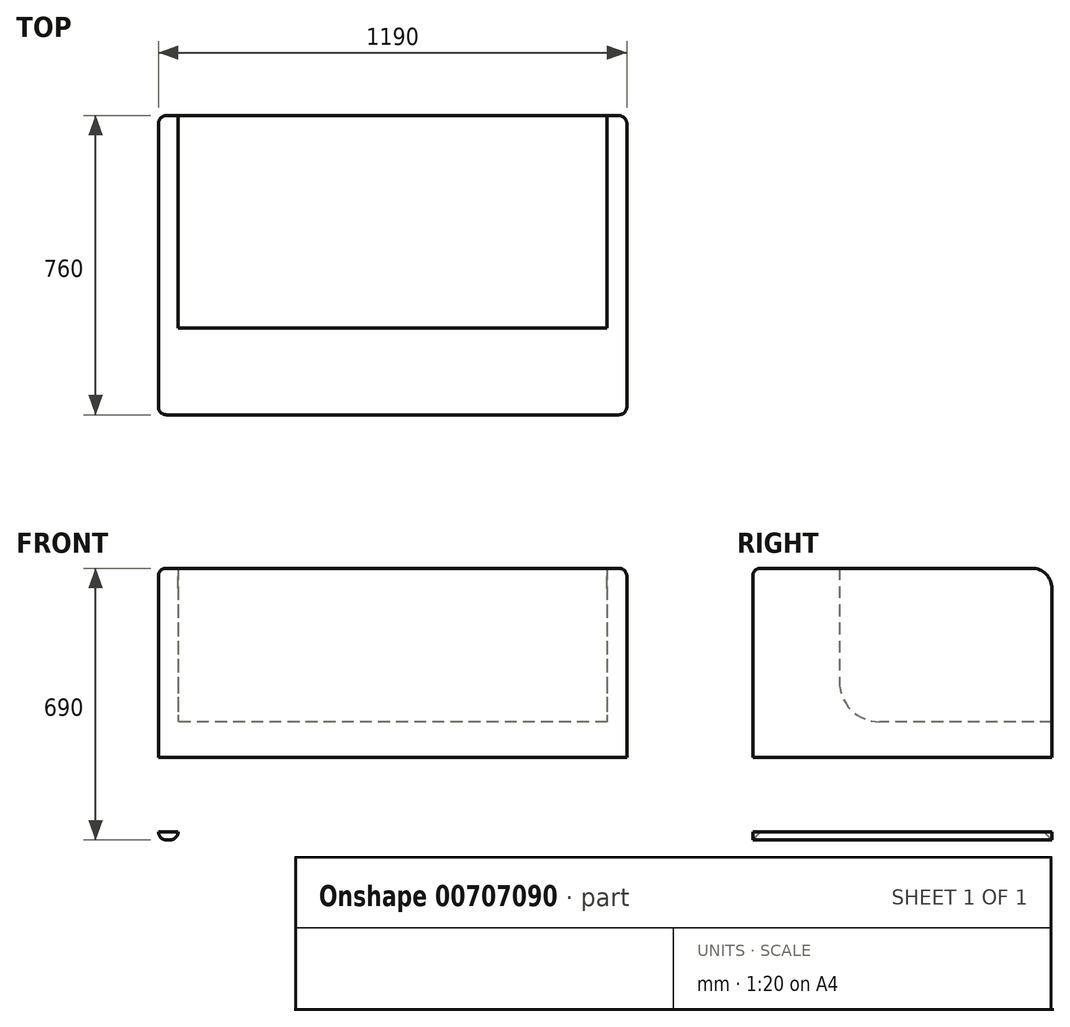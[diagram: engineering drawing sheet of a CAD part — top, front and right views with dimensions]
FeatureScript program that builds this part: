
annotation { "Feature Type Name" : "Feature", "Feature Type Description" : "" }
export const myFeature = defineFeature(function(context is Context, id is Id, definition is map)
    precondition{}
    {
        {
            var Q0;
            Q0=qCreatedBy(makeId("Right.planeOp"),FACE);
            var sketch = newSketch(context, id + "F0", { "sketchPlane" : qUnion([Q0])});
            skLineSegment(sketch, "E0", {"start": v(0, 0) * mm, "end": v(760, 0) * mm});
            skLineSegment(sketch, "E1", {"start": v(760, 0) * mm, "end": v(760, 690) * mm});
            skLineSegment(sketch, "E2", {"start": v(760, 690) * mm, "end": v(0, 690) * mm});
            skLineSegment(sketch, "E3", {"start": v(0, 690) * mm, "end": v(0, 0) * mm});
            skSolve(sketch);
        }
        {
            var Q0;
            Q0=makeQuery(id+"F0.imprint","IMPRINT",FACE,{"disambiguationData":[TD([[makeQuery(id+"F0.imprint","IMPRINT",EDGE,{"derivedFrom":sQuery(id+"F0.wireOp",EDGE,"E0")}),1.0]])]});
            extrude(context, id + "F1", {"entities" : qUnion([Q0]), "depth" : 1190 * mm});
        }
        {
            var Q0;
            Q0=makeQuery(id+"F1.opExtrude","SWEPT_FACE",FACE,{"disambiguationData":[OSD([sQuery(id+"F0.wireOp",EDGE,"E1")])]});
            var sketch = newSketch(context, id + "F2", { "sketchPlane" : qUnion([Q0])});
            skLineSegment(sketch, "E4.bottom", {"start": v(-1140, 0) * mm, "end": v(-50, 0) * mm});
            skLineSegment(sketch, "E4.top", {"start": v(-1140, 210) * mm, "end": v(-50, 210) * mm});
            skLineSegment(sketch, "E4.left", {"start": v(-1140, 0) * mm, "end": v(-1140, 210) * mm});
            skLineSegment(sketch, "E4.right", {"start": v(-50, 0) * mm, "end": v(-50, 210) * mm});
            skSolve(sketch);
        }
        {
            var Q0;
            Q0=makeQuery(id+"F2.imprint","IMPRINT",FACE,{"disambiguationData":[TD([[makeQuery(id+"F2.imprint","IMPRINT",EDGE,{"derivedFrom":sQuery(id+"F2.wireOp",EDGE,"E4.bottom")}),1.0]])]});
            var Q1;
            Q1=makeQuery(id+"F1.opExtrude","SWEPT_FACE",FACE,{"disambiguationData":[OSD([sQuery(id+"F0.wireOp",EDGE,"E3")])]});
            extrude(context, id + "F3", {"entities" : qUnion([Q0]), "operationType" : NewBodyOperationType.REMOVE, "endBound" : BoundingType.UP_TO_SURFACE, "oppositeDirection" : true, "endBoundEntityFace" : qUnion([Q1]), "depth" : 25.4 * mm});
        }
        {
            var Q0;
            Q0=qCreatedBy(makeId("Right.planeOp"),FACE);
            var sketch = newSketch(context, id + "F4", { "sketchPlane" : qUnion([Q0])});
            skPoint(sketch, "E5.0", {"position": v(760, 690) * mm});
            skLineSegment(sketch, "E6.bottom", {"start": v(760, 690) * mm, "end": v(220, 690) * mm});
            skLineSegment(sketch, "E6.top", {"start": v(760, 300) * mm, "end": v(220, 300) * mm});
            skLineSegment(sketch, "E6.left", {"start": v(760, 690) * mm, "end": v(760, 300) * mm});
            skLineSegment(sketch, "E6.right", {"start": v(220, 690) * mm, "end": v(220, 300) * mm});
            skSolve(sketch);
        }
        {
            var Q0;
            Q0=makeQuery(id+"F4.imprint","IMPRINT",FACE,{"disambiguationData":[TD([[makeQuery(id+"F4.imprint","IMPRINT",EDGE,{"derivedFrom":sQuery(id+"F4.wireOp",EDGE,"E6.bottom")}),1.0]])]});
            extrude(context, id + "F5", {"entities" : qUnion([Q0]), "operationType" : NewBodyOperationType.REMOVE, "depth" : 1140 * mm, "hasSecondDirection" : true, "secondDirectionOppositeDirection" : false, "secondDirectionDepth" : 50 * mm});
        }
        {
            var Q0;
            Q0=makeQuery(id+"F1.opExtrude","CAP_FACE",FACE,{"disambiguationData":[OSD([sQuery(id+"F0.wireOp",EDGE,"E0"),sQuery(id+"F0.wireOp",EDGE,"E1"),sQuery(id+"F0.wireOp",EDGE,"E2"),sQuery(id+"F0.wireOp",EDGE,"E3")])],"isStart":true});
            var Q1;
            Q1=makeQuery(id+"F1.opExtrude","CAP_FACE",FACE,{"disambiguationData":[OSD([sQuery(id+"F0.wireOp",EDGE,"E0"),sQuery(id+"F0.wireOp",EDGE,"E1"),sQuery(id+"F0.wireOp",EDGE,"E2"),sQuery(id+"F0.wireOp",EDGE,"E3")])],"isStart":false});
            var Q2;
            Q2=makeQuery(id+"F3.boolean.opBoolean","COPY",EDGE,{"derivedFrom":makeQuery(id+"F3.opExtrude","CAP_EDGE",EDGE,{"disambiguationData":[OSD([sQuery(id+"F2.wireOp",EDGE,"E4.left")])],"isStart":true})});
            var Q3;
            Q3=makeQuery(id+"F3.boolean.opBoolean","COPY",EDGE,{"derivedFrom":makeQuery(id+"F3.opExtrude","CAP_EDGE",EDGE,{"disambiguationData":[OSD([sQuery(id+"F2.wireOp",EDGE,"E4.right")])],"isStart":true})});
            var Q4;
            Q4=makeQuery(id+"F3.boolean.opBoolean","COPY",EDGE,{"derivedFrom":makeQuery(id+"F3.opExtrude","CAP_EDGE",EDGE,{"disambiguationData":[OSD([sQuery(id+"F2.wireOp",EDGE,"E4.right")])],"isStart":false})});
            var Q5;
            Q5=makeQuery(id+"F3.boolean.opBoolean","COPY",EDGE,{"derivedFrom":makeQuery(id+"F3.opExtrude","SWEPT_EDGE",EDGE,{"disambiguationData":[OSD([sQuery(id+"F0.wireOp",EDGE,"E0"),sQuery(id+"F0.wireOp",EDGE,"E1"),sQuery(id+"F2.wireOp",EDGE,"E4.bottom"),sQuery(id+"F2.wireOp",EDGE,"E4.right")])]})});
            var Q6;
            Q6=makeQuery(id+"F3.boolean.opBoolean","COPY",EDGE,{"derivedFrom":makeQuery(id+"F3.opExtrude","SWEPT_EDGE",EDGE,{"disambiguationData":[OSD([sQuery(id+"F0.wireOp",EDGE,"E0"),sQuery(id+"F0.wireOp",EDGE,"E1"),sQuery(id+"F2.wireOp",EDGE,"E4.bottom"),sQuery(id+"F2.wireOp",EDGE,"E4.left")])]})});
            var Q7;
            Q7=makeQuery(id+"F3.boolean.opBoolean","COPY",EDGE,{"derivedFrom":makeQuery(id+"F3.opExtrude","CAP_EDGE",EDGE,{"disambiguationData":[OSD([sQuery(id+"F2.wireOp",EDGE,"E4.top")])],"isStart":true})});
            var Q8;
            Q8=makeQuery(id+"F3.boolean.opBoolean","COPY",EDGE,{"derivedFrom":makeQuery(id+"F3.opExtrude","CAP_EDGE",EDGE,{"disambiguationData":[OSD([sQuery(id+"F2.wireOp",EDGE,"E4.top")])],"isStart":false})});
            var Q9;
            Q9=makeQuery(id+"F5.boolean.opBoolean","COPY",EDGE,{"derivedFrom":makeQuery(id+"F5.opExtrude","SWEPT_EDGE",EDGE,{"disambiguationData":[OSD([sQuery(id+"F4.wireOp",EDGE,"E6.top"),sQuery(id+"F4.wireOp",EDGE,"E6.left")])]})});
            var Q10;
            Q10=makeQuery(id+"F5.boolean.opBoolean","COPY",EDGE,{"derivedFrom":makeQuery(id+"F5.opExtrude","CAP_EDGE",EDGE,{"disambiguationData":[OSD([sQuery(id+"F4.wireOp",EDGE,"E6.left")])],"isStart":false})});
            var Q11;
            Q11=makeQuery(id+"F5.boolean.opBoolean","COPY",EDGE,{"derivedFrom":makeQuery(id+"F5.opExtrude","CAP_EDGE",EDGE,{"disambiguationData":[OSD([sQuery(id+"F4.wireOp",EDGE,"E6.bottom")])],"isStart":false})});
            var Q12;
            Q12=makeQuery(id+"F5.boolean.opBoolean","COPY",EDGE,{"derivedFrom":makeQuery(id+"F5.opExtrude","CAP_EDGE",EDGE,{"disambiguationData":[OSD([sQuery(id+"F4.wireOp",EDGE,"E6.bottom")])],"isStart":true})});
            var Q13;
            Q13=makeQuery(id+"F5.boolean.opBoolean","COPY",EDGE,{"derivedFrom":makeQuery(id+"F5.opExtrude","CAP_EDGE",EDGE,{"disambiguationData":[OSD([sQuery(id+"F4.wireOp",EDGE,"E6.left")])],"isStart":true})});
            var Q14;
            Q14=makeQuery(id+"F1.opExtrude","SWEPT_EDGE",EDGE,{"disambiguationData":[OSD([sQuery(id+"F0.wireOp",EDGE,"E2"),sQuery(id+"F0.wireOp",EDGE,"E3")])]});
            var Q15;
            Q15=makeQuery(id+"F3.boolean.opBoolean","COPY",EDGE,{"derivedFrom":makeQuery(id+"F3.opExtrude","CAP_EDGE",EDGE,{"disambiguationData":[OSD([sQuery(id+"F2.wireOp",EDGE,"E4.left")])],"isStart":false})});
            fillet(context, id + "F6", {"entities" : qUnion([Q0, Q1, Q2, Q3, Q4, Q5, Q6, Q7, Q8, Q9, Q10, Q11, Q12, Q13, Q14, Q15]), "radius" : 20.32 * mm, "tangentPropagation" : true, "allowEdgeOverflow" : false});
        }
        {
            var Q0;
            Q0=makeQuery(id+"F5.boolean.opBoolean","COPY",EDGE,{"derivedFrom":makeQuery(id+"F5.opExtrude","SWEPT_EDGE",EDGE,{"disambiguationData":[OSD([sQuery(id+"F4.wireOp",EDGE,"E6.bottom"),sQuery(id+"F4.wireOp",EDGE,"E6.right")])]})});
            var Q1;
            Q1=makeQuery(id+"F5.boolean.opBoolean","COPY",EDGE,{"derivedFrom":makeQuery(id+"F5.opExtrude","SWEPT_EDGE",EDGE,{"disambiguationData":[OSD([sQuery(id+"F4.wireOp",EDGE,"E6.top"),sQuery(id+"F4.wireOp",EDGE,"E6.right")])]})});
            fillet(context, id + "F7", {"entities" : qUnion([Q0, Q1]), "radius" : 101.6 * mm, "tangentPropagation" : true, "allowEdgeOverflow" : false});
        }
        {
            var Q0;
            Q0=makeQuery(id+"F3.boolean.opBoolean","COPY",FACE,{"derivedFrom":makeQuery(id+"F3.opExtrude","SWEPT_FACE",FACE,{"disambiguationData":[OSD([sQuery(id+"F2.wireOp",EDGE,"E4.left")])]})});
            var Q1;
            Q1=makeQuery(id+"F1.opExtrude","CAP_FACE",FACE,{"disambiguationData":[OSD([sQuery(id+"F0.wireOp",EDGE,"E0"),sQuery(id+"F0.wireOp",EDGE,"E1"),sQuery(id+"F0.wireOp",EDGE,"E2"),sQuery(id+"F0.wireOp",EDGE,"E3")])],"isStart":false});
            extrude(context, id + "F8", {"entities" : qUnion([Q0]), "operationType" : NewBodyOperationType.REMOVE, "endBound" : BoundingType.UP_TO_SURFACE, "oppositeDirection" : true, "endBoundEntityFace" : qUnion([Q1]), "depth" : 25.4 * mm});
        }
        {
            var Q0;
            Q0=makeQuery(id+"F3.boolean.opBoolean","COPY",FACE,{"derivedFrom":makeQuery(id+"F3.opExtrude","SWEPT_FACE",FACE,{"disambiguationData":[OSD([sQuery(id+"F2.wireOp",EDGE,"E4.right")])]})});
            var Q1;
            Q1=makeQuery(id+"F1.opExtrude","CAP_FACE",FACE,{"disambiguationData":[OSD([sQuery(id+"F0.wireOp",EDGE,"E0"),sQuery(id+"F0.wireOp",EDGE,"E1"),sQuery(id+"F0.wireOp",EDGE,"E2"),sQuery(id+"F0.wireOp",EDGE,"E3")])],"isStart":true});
            extrude(context, id + "F9", {"entities" : qUnion([Q0]), "operationType" : NewBodyOperationType.REMOVE, "endBound" : BoundingType.UP_TO_SURFACE, "oppositeDirection" : true, "endBoundEntityFace" : qUnion([Q1]), "depth" : 25.4 * mm});
        }
        {
            var Q0;
            {var subQ0=sQuery(id+"F0.wireOp",EDGE,"E2");var subQ1=sQuery(id+"F0.wireOp",EDGE,"E1");Q0=makeQuery(id+"F5.boolean.opBoolean","SPLIT",EDGE,{"disambiguationData":[TD([makeQuery(id+"F1.opExtrude","CAP_FACE",FACE,{"disambiguationData":[OSD([sQuery(id+"F0.wireOp",EDGE,"E0"),subQ1,subQ0,sQuery(id+"F0.wireOp",EDGE,"E3")])],"isStart":false})])],"derivedFrom":makeQuery(id+"F1.opExtrude","SWEPT_EDGE",EDGE,{"disambiguationData":[OSD([subQ1,subQ0])]})});}
            var Q1;
            {var subQ0=sQuery(id+"F0.wireOp",EDGE,"E2");var subQ1=sQuery(id+"F0.wireOp",EDGE,"E1");Q1=makeQuery(id+"F5.boolean.opBoolean","SPLIT",EDGE,{"disambiguationData":[TD([makeQuery(id+"F1.opExtrude","CAP_FACE",FACE,{"disambiguationData":[OSD([sQuery(id+"F0.wireOp",EDGE,"E0"),subQ1,subQ0,sQuery(id+"F0.wireOp",EDGE,"E3")])],"isStart":true})])],"derivedFrom":makeQuery(id+"F1.opExtrude","SWEPT_EDGE",EDGE,{"disambiguationData":[OSD([subQ1,subQ0])]})});}
            var Q2;
            {var subQ0=sQuery(id+"F2.wireOp",EDGE,"E4.right");var subQ1=sQuery(id+"F2.wireOp",EDGE,"E4.bottom");var subQ2=sQuery(id+"F0.wireOp",EDGE,"E1");var subQ3=sQuery(id+"F0.wireOp",EDGE,"E0");Q2=makeQuery(id+"F9.boolean.opBoolean","COPY",EDGE,{"derivedFrom":makeQuery(id+"F9.opExtrude","SWEPT_EDGE",EDGE,{"disambiguationData":[OSD([subQ3,subQ2,subQ1,subQ0]),TDD([makeQuery(id+"F6.opFillet","BLEND_VERTEX",VERTEX,{"blendedFrom":[makeQuery(id+"F3.boolean.opBoolean","COPY",EDGE,{"derivedFrom":makeQuery(id+"F3.opExtrude","SWEPT_EDGE",EDGE,{"disambiguationData":[OSD([subQ3,subQ2,subQ1,subQ0])]})}),makeQuery(id+"F3.boolean.opBoolean","COPY",EDGE,{"derivedFrom":makeQuery(id+"F3.opExtrude","CAP_EDGE",EDGE,{"disambiguationData":[OSD([subQ0])],"isStart":true})}),makeQuery(id+"F3.boolean.opBoolean","COPY",FACE,{"derivedFrom":makeQuery(id+"F3.opExtrude","SWEPT_FACE",FACE,{"disambiguationData":[OSD([subQ0])]})})],"blendedInto":[makeQuery(id+"F3.boolean.opBoolean","COPY",FACE,{"derivedFrom":makeQuery(id+"F3.opExtrude","SWEPT_FACE",FACE,{"disambiguationData":[OSD([subQ0])]})})]})])]})});}
            var Q3;
            {var subQ0=sQuery(id+"F2.wireOp",EDGE,"E4.right");var subQ1=sQuery(id+"F2.wireOp",EDGE,"E4.bottom");var subQ2=sQuery(id+"F0.wireOp",EDGE,"E1");var subQ3=sQuery(id+"F0.wireOp",EDGE,"E0");Q3=makeQuery(id+"F9.boolean.opBoolean","COPY",EDGE,{"derivedFrom":makeQuery(id+"F9.opExtrude","SWEPT_EDGE",EDGE,{"disambiguationData":[OSD([subQ3,subQ2,subQ1,subQ0]),TDD([makeQuery(id+"F6.opFillet","BLEND_VERTEX",VERTEX,{"blendedFrom":[makeQuery(id+"F3.boolean.opBoolean","COPY",EDGE,{"derivedFrom":makeQuery(id+"F3.opExtrude","SWEPT_EDGE",EDGE,{"disambiguationData":[OSD([subQ3,subQ2,subQ1,subQ0])]})}),makeQuery(id+"F3.boolean.opBoolean","COPY",EDGE,{"derivedFrom":makeQuery(id+"F3.opExtrude","CAP_EDGE",EDGE,{"disambiguationData":[OSD([subQ0])],"isStart":false})}),makeQuery(id+"F3.boolean.opBoolean","COPY",FACE,{"derivedFrom":makeQuery(id+"F3.opExtrude","SWEPT_FACE",FACE,{"disambiguationData":[OSD([subQ0])]})})],"blendedInto":[makeQuery(id+"F3.boolean.opBoolean","COPY",FACE,{"derivedFrom":makeQuery(id+"F3.opExtrude","SWEPT_FACE",FACE,{"disambiguationData":[OSD([subQ0])]})})]})])]})});}
            var Q4;
            {var subQ0=sQuery(id+"F2.wireOp",EDGE,"E4.left");var subQ1=sQuery(id+"F2.wireOp",EDGE,"E4.bottom");var subQ2=sQuery(id+"F0.wireOp",EDGE,"E1");var subQ3=sQuery(id+"F0.wireOp",EDGE,"E0");Q4=makeQuery(id+"F8.boolean.opBoolean","COPY",EDGE,{"derivedFrom":makeQuery(id+"F8.opExtrude","SWEPT_EDGE",EDGE,{"disambiguationData":[OSD([subQ3,subQ2,subQ1,subQ0]),TDD([makeQuery(id+"F6.opFillet","BLEND_VERTEX",VERTEX,{"blendedFrom":[makeQuery(id+"F3.boolean.opBoolean","COPY",EDGE,{"derivedFrom":makeQuery(id+"F3.opExtrude","SWEPT_EDGE",EDGE,{"disambiguationData":[OSD([subQ3,subQ2,subQ1,subQ0])]})}),makeQuery(id+"F3.boolean.opBoolean","COPY",EDGE,{"derivedFrom":makeQuery(id+"F3.opExtrude","CAP_EDGE",EDGE,{"disambiguationData":[OSD([subQ0])],"isStart":false})}),makeQuery(id+"F3.boolean.opBoolean","COPY",FACE,{"derivedFrom":makeQuery(id+"F3.opExtrude","SWEPT_FACE",FACE,{"disambiguationData":[OSD([subQ0])]})})],"blendedInto":[makeQuery(id+"F3.boolean.opBoolean","COPY",FACE,{"derivedFrom":makeQuery(id+"F3.opExtrude","SWEPT_FACE",FACE,{"disambiguationData":[OSD([subQ0])]})})]})])]})});}
            var Q5;
            {var subQ0=sQuery(id+"F2.wireOp",EDGE,"E4.left");var subQ1=sQuery(id+"F2.wireOp",EDGE,"E4.bottom");var subQ2=sQuery(id+"F0.wireOp",EDGE,"E1");var subQ3=sQuery(id+"F0.wireOp",EDGE,"E0");Q5=makeQuery(id+"F8.boolean.opBoolean","COPY",EDGE,{"derivedFrom":makeQuery(id+"F8.opExtrude","SWEPT_EDGE",EDGE,{"disambiguationData":[OSD([subQ3,subQ2,subQ1,subQ0]),TDD([makeQuery(id+"F6.opFillet","BLEND_VERTEX",VERTEX,{"blendedFrom":[makeQuery(id+"F3.boolean.opBoolean","COPY",EDGE,{"derivedFrom":makeQuery(id+"F3.opExtrude","SWEPT_EDGE",EDGE,{"disambiguationData":[OSD([subQ3,subQ2,subQ1,subQ0])]})}),makeQuery(id+"F3.boolean.opBoolean","COPY",EDGE,{"derivedFrom":makeQuery(id+"F3.opExtrude","CAP_EDGE",EDGE,{"disambiguationData":[OSD([subQ0])],"isStart":true})}),makeQuery(id+"F3.boolean.opBoolean","COPY",FACE,{"derivedFrom":makeQuery(id+"F3.opExtrude","SWEPT_FACE",FACE,{"disambiguationData":[OSD([subQ0])]})})],"blendedInto":[makeQuery(id+"F3.boolean.opBoolean","COPY",FACE,{"derivedFrom":makeQuery(id+"F3.opExtrude","SWEPT_FACE",FACE,{"disambiguationData":[OSD([subQ0])]})})]})])]})});}
            fillet(context, id + "F10", {"entities" : qUnion([Q0, Q1, Q2, Q3, Q4, Q5]), "radius" : 50.8 * mm, "tangentPropagation" : true, "allowEdgeOverflow" : false});
        }
    });
